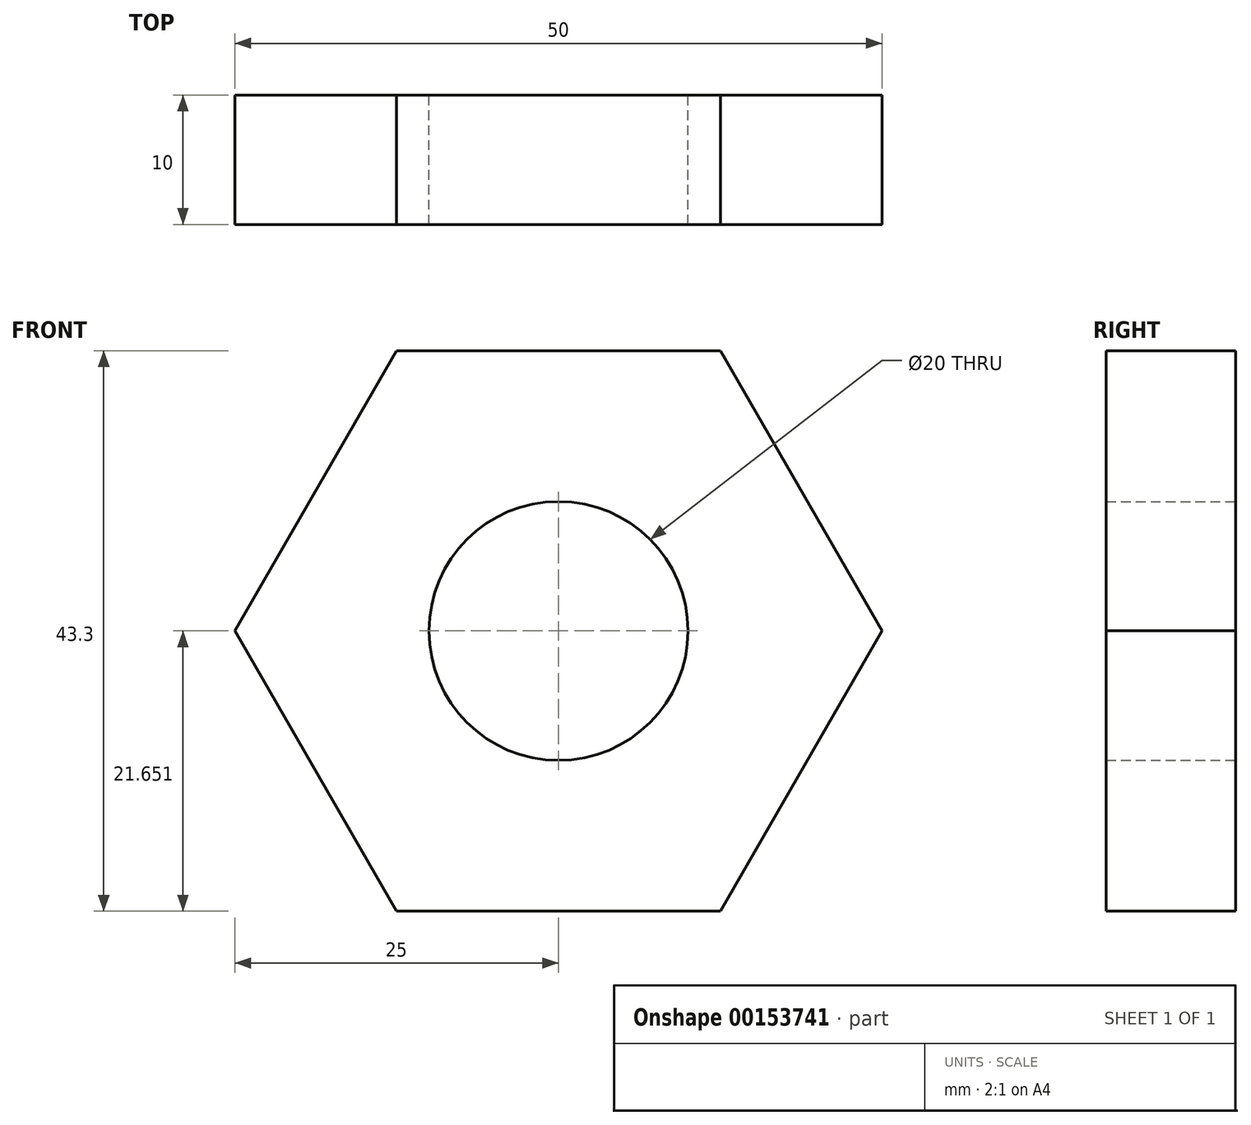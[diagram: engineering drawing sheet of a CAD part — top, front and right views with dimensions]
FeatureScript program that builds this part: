
annotation { "Feature Type Name" : "Feature", "Feature Type Description" : "" }
export const myFeature = defineFeature(function(context is Context, id is Id, definition is map)
    precondition{}
    {
        {
            var Q0;
            Q0=qCreatedBy(makeId("Front.planeOp"),FACE);
            var sketch = newSketch(context, id + "F0", { "sketchPlane" : qUnion([Q0])});
            skLineSegment(sketch, "E0", {"start": v(-12.5, 0) * mm, "end": v(12.5, 0) * mm});
            skLineSegment(sketch, "E1", {"start": v(12.5, 0) * mm, "end": v(25, 21.65) * mm});
            skLineSegment(sketch, "E2", {"start": v(25, 21.65) * mm, "end": v(12.5, 43.3) * mm});
            skLineSegment(sketch, "E3", {"start": v(12.5, 43.3) * mm, "end": v(-12.5, 43.3) * mm});
            skLineSegment(sketch, "E4", {"start": v(-12.5, 43.3) * mm, "end": v(-25, 21.65) * mm});
            skLineSegment(sketch, "E5", {"start": v(-25, 21.65) * mm, "end": v(-12.5, 0) * mm});
            skCircle(sketch, "E6", {"center": v(0, 21.65) * mm, "radius": 10 * mm});
            skSolve(sketch);
        }
        {
            var Q0;
            Q0 = qSketchRegion(id + "F0", true);
            extrude(context, id + "F1", {"entities" : qUnion([Q0]), "depth" : 10 * mm});
        }
    });
